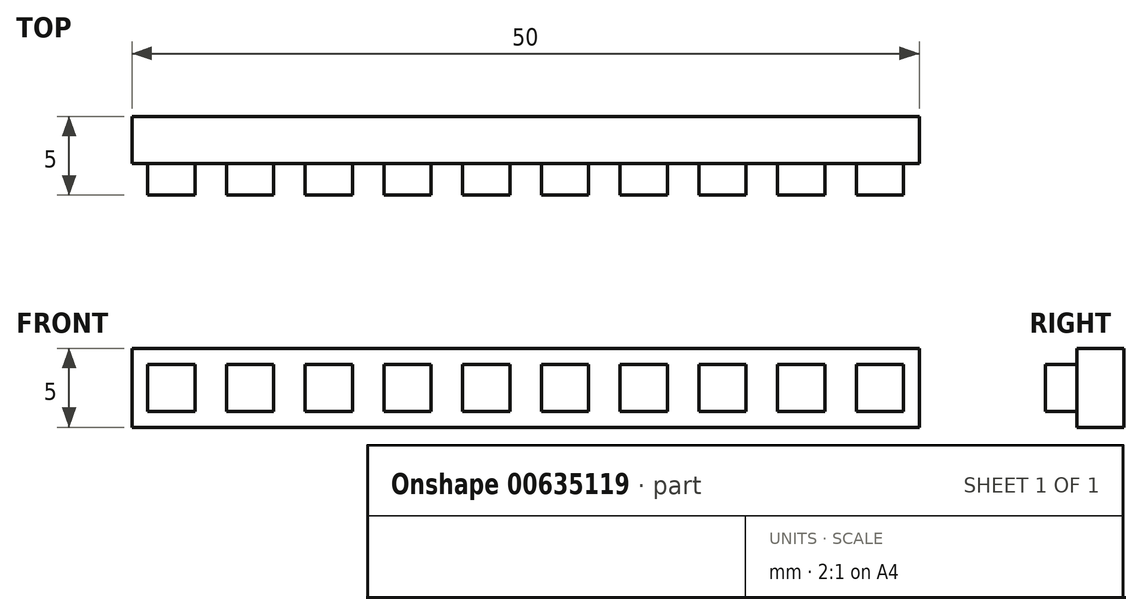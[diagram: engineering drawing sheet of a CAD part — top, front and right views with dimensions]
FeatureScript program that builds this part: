
annotation { "Feature Type Name" : "Feature", "Feature Type Description" : "" }
export const myFeature = defineFeature(function(context is Context, id is Id, definition is map)
    precondition{}
    {
        {
            var Q0;
            Q0=qCreatedBy(makeId("Front.planeOp"),FACE);
            var sketch = newSketch(context, id + "F0", { "sketchPlane" : qUnion([Q0])});
            skLineSegment(sketch, "E0.bottom", {"start": v(-25, -2.5) * mm, "end": v(25, -2.5) * mm});
            skLineSegment(sketch, "E0.top", {"start": v(-25, 2.5) * mm, "end": v(25, 2.5) * mm});
            skLineSegment(sketch, "E0.left", {"start": v(-25, -2.5) * mm, "end": v(-25, 2.5) * mm});
            skLineSegment(sketch, "E0.right", {"start": v(25, -2.5) * mm, "end": v(25, 2.5) * mm});
            skPoint(sketch, "E0.middle", {"position": v(0, 0) * mm});
            skSolve(sketch);
        }
        {
            var Q0;
            Q0 = qSketchRegion(id + "F0", true);
            extrude(context, id + "F1", {"entities" : qUnion([Q0]), "depth" : 3 * mm, "offsetDistance" : 25.4 * mm});
        }
        {
            var Q0;
            Q0=makeQuery(id+"F1.opExtrude","CAP_FACE",FACE,{"disambiguationData":[OSD([sQuery(id+"F0.wireOp",EDGE,"E0.bottom"),sQuery(id+"F0.wireOp",EDGE,"E0.top"),sQuery(id+"F0.wireOp",EDGE,"E0.left"),sQuery(id+"F0.wireOp",EDGE,"E0.right")])],"isStart":false});
            var sketch = newSketch(context, id + "F2", { "sketchPlane" : qUnion([Q0])});
            skLineSegment(sketch, "E1.bottom", {"start": v(-21, -1.5) * mm, "end": v(-24, -1.5) * mm});
            skLineSegment(sketch, "E1.top", {"start": v(-21, 1.5) * mm, "end": v(-24, 1.5) * mm});
            skLineSegment(sketch, "E1.left", {"start": v(-21, -1.5) * mm, "end": v(-21, 1.5) * mm});
            skLineSegment(sketch, "E1.right", {"start": v(-24, -1.5) * mm, "end": v(-24, 1.5) * mm});
            skPoint(sketch, "E1.middle", {"position": v(-22.5, 0) * mm});
            skPoint(sketch, "E1.middle.positionSnap0", {"position": v(-25, 0) * mm});
            skPoint(sketch, "E1.centerSnap0", {"position": v(-25, 0) * mm});
            skLineSegment(sketch, "E2.1.0.0", {"start": v(-19, -1.5) * mm, "end": v(-19, 1.5) * mm});
            skLineSegment(sketch, "E2.1.0.1", {"start": v(-16, 1.5) * mm, "end": v(-19, 1.5) * mm});
            skLineSegment(sketch, "E2.1.0.2", {"start": v(-16, -1.5) * mm, "end": v(-16, 1.5) * mm});
            skLineSegment(sketch, "E2.1.0.3", {"start": v(-16, -1.5) * mm, "end": v(-19, -1.5) * mm});
            skLineSegment(sketch, "E2.2.0.0", {"start": v(-14, -1.5) * mm, "end": v(-14, 1.5) * mm});
            skLineSegment(sketch, "E2.2.0.1", {"start": v(-11, 1.5) * mm, "end": v(-14, 1.5) * mm});
            skLineSegment(sketch, "E2.2.0.2", {"start": v(-11, -1.5) * mm, "end": v(-11, 1.5) * mm});
            skLineSegment(sketch, "E2.2.0.3", {"start": v(-11, -1.5) * mm, "end": v(-14, -1.5) * mm});
            skLineSegment(sketch, "E2.3.0.0", {"start": v(-9, -1.5) * mm, "end": v(-9, 1.5) * mm});
            skLineSegment(sketch, "E2.3.0.1", {"start": v(-6, 1.5) * mm, "end": v(-9, 1.5) * mm});
            skLineSegment(sketch, "E2.3.0.2", {"start": v(-6, -1.5) * mm, "end": v(-6, 1.5) * mm});
            skLineSegment(sketch, "E2.3.0.3", {"start": v(-6, -1.5) * mm, "end": v(-9, -1.5) * mm});
            skLineSegment(sketch, "E2.4.0.0", {"start": v(-4, -1.5) * mm, "end": v(-4, 1.5) * mm});
            skLineSegment(sketch, "E2.4.0.1", {"start": v(-1, 1.5) * mm, "end": v(-4, 1.5) * mm});
            skLineSegment(sketch, "E2.4.0.2", {"start": v(-1, -1.5) * mm, "end": v(-1, 1.5) * mm});
            skLineSegment(sketch, "E2.4.0.3", {"start": v(-1, -1.5) * mm, "end": v(-4, -1.5) * mm});
            skLineSegment(sketch, "E2.5.0.0", {"start": v(1, -1.5) * mm, "end": v(1, 1.5) * mm});
            skLineSegment(sketch, "E2.5.0.1", {"start": v(4, 1.5) * mm, "end": v(1, 1.5) * mm});
            skLineSegment(sketch, "E2.5.0.2", {"start": v(4, -1.5) * mm, "end": v(4, 1.5) * mm});
            skLineSegment(sketch, "E2.5.0.3", {"start": v(4, -1.5) * mm, "end": v(1, -1.5) * mm});
            skLineSegment(sketch, "E2.6.0.0", {"start": v(6, -1.5) * mm, "end": v(6, 1.5) * mm});
            skLineSegment(sketch, "E2.6.0.1", {"start": v(9, 1.5) * mm, "end": v(6, 1.5) * mm});
            skLineSegment(sketch, "E2.6.0.2", {"start": v(9, -1.5) * mm, "end": v(9, 1.5) * mm});
            skLineSegment(sketch, "E2.6.0.3", {"start": v(9, -1.5) * mm, "end": v(6, -1.5) * mm});
            skLineSegment(sketch, "E2.7.0.0", {"start": v(11, -1.5) * mm, "end": v(11, 1.5) * mm});
            skLineSegment(sketch, "E2.7.0.1", {"start": v(14, 1.5) * mm, "end": v(11, 1.5) * mm});
            skLineSegment(sketch, "E2.7.0.2", {"start": v(14, -1.5) * mm, "end": v(14, 1.5) * mm});
            skLineSegment(sketch, "E2.7.0.3", {"start": v(14, -1.5) * mm, "end": v(11, -1.5) * mm});
            skLineSegment(sketch, "E2.8.0.0", {"start": v(16, -1.5) * mm, "end": v(16, 1.5) * mm});
            skLineSegment(sketch, "E2.8.0.1", {"start": v(19, 1.5) * mm, "end": v(16, 1.5) * mm});
            skLineSegment(sketch, "E2.8.0.2", {"start": v(19, -1.5) * mm, "end": v(19, 1.5) * mm});
            skLineSegment(sketch, "E2.8.0.3", {"start": v(19, -1.5) * mm, "end": v(16, -1.5) * mm});
            skLineSegment(sketch, "E2.9.0.0", {"start": v(21, -1.5) * mm, "end": v(21, 1.5) * mm});
            skLineSegment(sketch, "E2.9.0.1", {"start": v(24, 1.5) * mm, "end": v(21, 1.5) * mm});
            skLineSegment(sketch, "E2.9.0.2", {"start": v(24, -1.5) * mm, "end": v(24, 1.5) * mm});
            skLineSegment(sketch, "E2.9.0.3", {"start": v(24, -1.5) * mm, "end": v(21, -1.5) * mm});
            skLineSegment(sketch, "E2.direction1", {"start": v(-24, -1.5) * mm, "end": v(-19, -1.5) * mm, "construction": true});
            skSolve(sketch);
        }
        {
            var Q0;
            Q0=makeQuery(id+"F2.imprint","IMPRINT",FACE,{"disambiguationData":[TD([[makeQuery(id+"F2.imprint","IMPRINT",EDGE,{"derivedFrom":sQuery(id+"F2.wireOp",EDGE,"E1.bottom")}),-1.0]])]});
            var Q1;
            Q1=makeQuery(id+"F2.imprint","IMPRINT",FACE,{"disambiguationData":[TD([[makeQuery(id+"F2.imprint","IMPRINT",EDGE,{"derivedFrom":sQuery(id+"F2.wireOp",EDGE,"E2.1.0.0")}),-1.0]])]});
            var Q2;
            Q2=makeQuery(id+"F2.imprint","IMPRINT",FACE,{"disambiguationData":[TD([[makeQuery(id+"F2.imprint","IMPRINT",EDGE,{"derivedFrom":sQuery(id+"F2.wireOp",EDGE,"E2.2.0.0")}),-1.0]])]});
            var Q3;
            Q3=makeQuery(id+"F2.imprint","IMPRINT",FACE,{"disambiguationData":[TD([[makeQuery(id+"F2.imprint","IMPRINT",EDGE,{"derivedFrom":sQuery(id+"F2.wireOp",EDGE,"E2.3.0.0")}),-1.0]])]});
            var Q4;
            Q4=makeQuery(id+"F2.imprint","IMPRINT",FACE,{"disambiguationData":[TD([[makeQuery(id+"F2.imprint","IMPRINT",EDGE,{"derivedFrom":sQuery(id+"F2.wireOp",EDGE,"E2.4.0.0")}),-1.0]])]});
            var Q5;
            Q5=makeQuery(id+"F2.imprint","IMPRINT",FACE,{"disambiguationData":[TD([[makeQuery(id+"F2.imprint","IMPRINT",EDGE,{"derivedFrom":sQuery(id+"F2.wireOp",EDGE,"E2.5.0.0")}),-1.0]])]});
            var Q6;
            Q6=makeQuery(id+"F2.imprint","IMPRINT",FACE,{"disambiguationData":[TD([[makeQuery(id+"F2.imprint","IMPRINT",EDGE,{"derivedFrom":sQuery(id+"F2.wireOp",EDGE,"E2.6.0.0")}),-1.0]])]});
            var Q7;
            Q7=makeQuery(id+"F2.imprint","IMPRINT",FACE,{"disambiguationData":[TD([[makeQuery(id+"F2.imprint","IMPRINT",EDGE,{"derivedFrom":sQuery(id+"F2.wireOp",EDGE,"E2.7.0.0")}),-1.0]])]});
            var Q8;
            Q8=makeQuery(id+"F2.imprint","IMPRINT",FACE,{"disambiguationData":[TD([[makeQuery(id+"F2.imprint","IMPRINT",EDGE,{"derivedFrom":sQuery(id+"F2.wireOp",EDGE,"E2.8.0.0")}),-1.0]])]});
            var Q9;
            Q9=makeQuery(id+"F2.imprint","IMPRINT",FACE,{"disambiguationData":[TD([[makeQuery(id+"F2.imprint","IMPRINT",EDGE,{"derivedFrom":sQuery(id+"F2.wireOp",EDGE,"E2.9.0.0")}),-1.0]])]});
            extrude(context, id + "F3", {"entities" : qUnion([Q0, Q1, Q2, Q3, Q4, Q5, Q6, Q7, Q8, Q9]), "operationType" : NewBodyOperationType.ADD, "depth" : 2 * mm, "offsetDistance" : 25 * mm});
        }
    });
